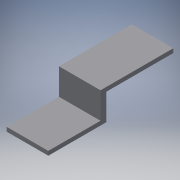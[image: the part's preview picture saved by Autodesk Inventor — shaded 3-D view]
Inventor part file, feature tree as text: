
AUTODESK INVENTOR PART (.ipt)
format: ipt  version: 2018 (Build 220112000, 112)  size: 120,832 bytes
history: native  units: mm
features: extrude x3, sketch x3, reference x3, other x3, plane x2
ambient origin geometry x8: Origin, YZ Plane, XZ Plane, XY Plane, X Axis, Y Axis, Z Axis, Center Point
bodies: Solid1 (feature_tree)
feature tree (14):
  extrude  "Extrusion1"  Depth=20.0mm
  sketch  "Sketch2"  dims[d2=35.0mm d3=2.0mm d4=0.0mm]
  plane  "Work Plane1"
  extrude  "Extrusion2"  Depth=2.0mm TaperAngle=0.0deg
  sketch  "Sketch3"  dims[d5=2.0mm d6=0.0mm d7=2.0mm d8=2.0mm d9=0.0mm]
  plane  "Work Plane2"
  extrude  "Extrusion3"  Depth=2.0mm
  sketch  "Sketch1"  dims[d0=10.0mm d1=20.0mm]
  reference  "Reference1"
  reference  "Reference2"
  reference  "Reference3"
  other  "<userpath>\OneDrive\Documents\Inventor\TSA\2018\Animatronics\Tortoise\Head\HeadAssembly.iam"
  other  "HeadAssembly.iam"
  other  "HeadBottom:1"
